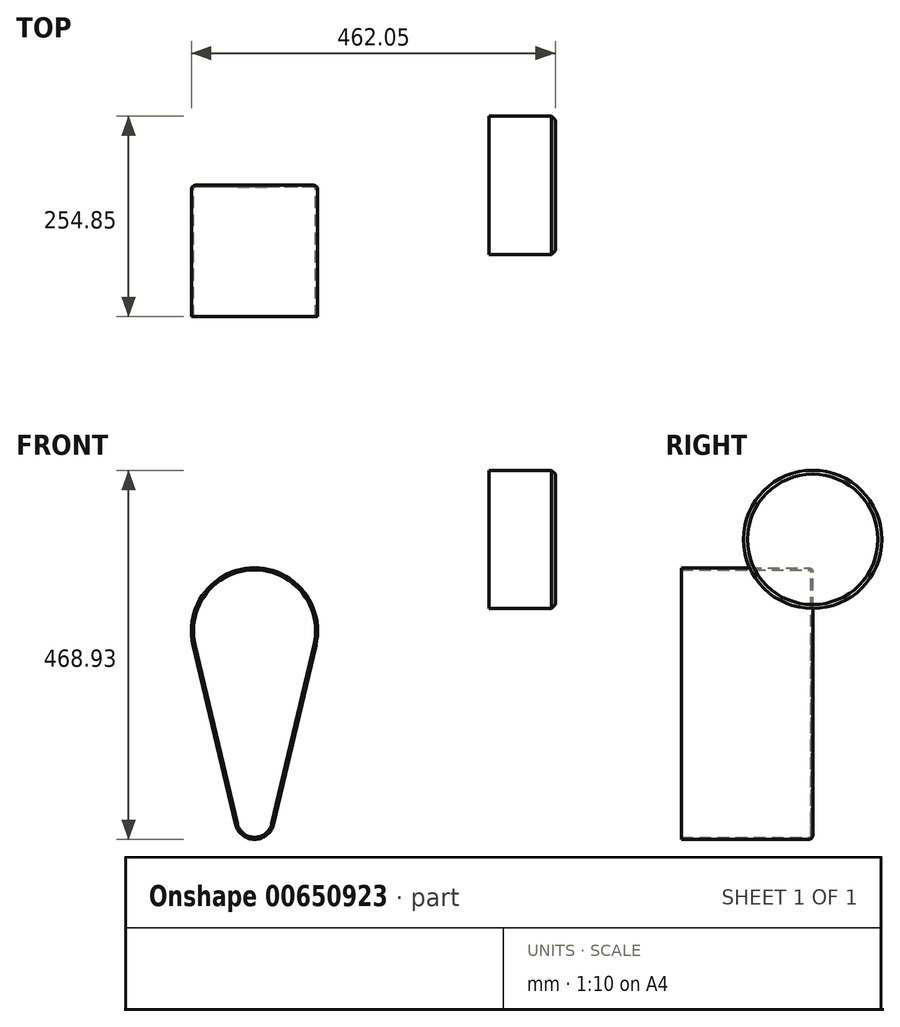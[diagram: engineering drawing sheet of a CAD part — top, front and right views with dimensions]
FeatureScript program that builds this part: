
annotation { "Feature Type Name" : "Feature", "Feature Type Description" : "" }
export const myFeature = defineFeature(function(context is Context, id is Id, definition is map)
    precondition{}
    {
        {
            var Q0;
            Q0=qCreatedBy(makeId("Front.planeOp"),FACE);
            var sketch = newSketch(context, id + "F0", { "sketchPlane" : qUnion([Q0])});
            skLineSegment(sketch, "E0.bottom", {"start": v(-42.05, 43.93) * mm, "end": v(42.05, 43.93) * mm});
            skLineSegment(sketch, "E0.top", {"start": v(-42.05, -43.93) * mm, "end": v(42.05, -43.93) * mm});
            skLineSegment(sketch, "E0.left", {"start": v(-42.05, 43.93) * mm, "end": v(-42.05, -43.93) * mm});
            skLineSegment(sketch, "E0.right", {"start": v(42.05, 43.93) * mm, "end": v(42.05, -43.93) * mm});
            skPoint(sketch, "E0.middle", {"position": v(0, 0) * mm});
            skSolve(sketch);
        }
        {
            var Q0;
            Q0=qCreatedBy(makeId("Front.planeOp"),FACE);
            var sketch = newSketch(context, id + "F1", { "sketchPlane" : qUnion([Q0])});
            skLineSegment(sketch, "E1.bottom", {"start": v(-150, 75) * mm, "end": v(150, 75) * mm});
            skLineSegment(sketch, "E1.top", {"start": v(-150, -75) * mm, "end": v(150, -75) * mm});
            skLineSegment(sketch, "E1.left", {"start": v(-150, 75) * mm, "end": v(-150, -75) * mm});
            skLineSegment(sketch, "E1.right", {"start": v(150, 75) * mm, "end": v(150, -75) * mm});
            skPoint(sketch, "E1.middle", {"position": v(0, 0) * mm});
            skCircle(sketch, "E2", {"center": v(0, 0) * mm, "radius": 50 * mm});
            skArc(sketch, "E3", {"start": v(-262.13, -178.33) * mm, "mid": v(-340, -80) * mm, "end": v(-417.87, -178.33) * mm});
            skArc(sketch, "E4", {"start": v(-364.33, -405.73) * mm, "mid": v(-340, -425) * mm, "end": v(-315.67, -405.73) * mm});
            skLineSegment(sketch, "E5", {"start": v(-262.13, -178.33) * mm, "end": v(-315.67, -405.73) * mm});
            skLineSegment(sketch, "E6", {"start": v(-364.33, -405.73) * mm, "end": v(-417.87, -178.33) * mm});
            skLineSegment(sketch, "E7", {"start": v(-340, -160) * mm, "end": v(-340, -400) * mm, "construction": true});
            skCircle(sketch, "E8", {"center": v(0, 0) * mm, "radius": 62.34 * mm, "construction": true});
            skCircle(sketch, "E9", {"center": v(-99, 57.26) * mm, "radius": 7.58 * mm});
            skSolve(sketch);
        }
        {
            var Q0;
            Q0=makeQuery(id+"F1.imprint","IMPRINT",FACE,{"disambiguationData":[TD([[makeQuery(id+"F1.imprint","IMPRINT",EDGE,{"derivedFrom":sQuery(id+"F1.wireOp",EDGE,"E3")}),1.0]])]});
            extrude(context, id + "F2", {"entities" : qUnion([Q0]), "depth" : 167 * mm, "offsetDistance" : 25 * mm});
        }
        {
            var Q0;
            Q0=makeQuery(id+"F0.imprint","IMPRINT",FACE,{"disambiguationData":[TD([[makeQuery(id+"F0.imprint","IMPRINT",EDGE,{"derivedFrom":sQuery(id+"F0.wireOp",EDGE,"E0.bottom")}),-1.0]])]});
            var Q1;
            Q1=sQuery(id+"F0.wireOp",EDGE,"E0.top");
            revolve(context, id + "F3", {"entities" : qUnion([Q0]), "axis" : qUnion([Q1]), "revolveType" : RevolveType.FULL});
        }
        {
            var Q0;
            Q0=makeQuery(id+"F2.opExtrude","CAP_FACE",FACE,{"disambiguationData":[OSD([sQuery(id+"F1.wireOp",EDGE,"E3"),sQuery(id+"F1.wireOp",EDGE,"E4"),sQuery(id+"F1.wireOp",EDGE,"E5"),sQuery(id+"F1.wireOp",EDGE,"E6")])],"isStart":false});
            shell(context, id + "F4", {"entities" : qUnion([Q0]), "thickness" : 2.5 * mm});
        }
        {
            var Q0;
            Q0=makeQuery(id+"F2.opExtrude","CAP_EDGE",EDGE,{"disambiguationData":[OSD([sQuery(id+"F1.wireOp",EDGE,"E5")])],"isStart":true});
            fillet(context, id + "F5", {"entities" : qUnion([Q0]), "radius" : 5 * mm, "tangentPropagation" : true, "allowEdgeOverflow" : false});
        }
        {
            var Q0;
            Q0=makeQuery(id+"F3.opRevolve","SWEPT_EDGE",EDGE,{"disambiguationData":[OSD([sQuery(id+"F0.wireOp",EDGE,"E0.bottom"),sQuery(id+"F0.wireOp",EDGE,"E0.right")])]});
            chamfer(context, id + "F6", {"entities" : qUnion([Q0]), "width" : 5 * mm, "tangentPropagation" : true});
        }
    });
